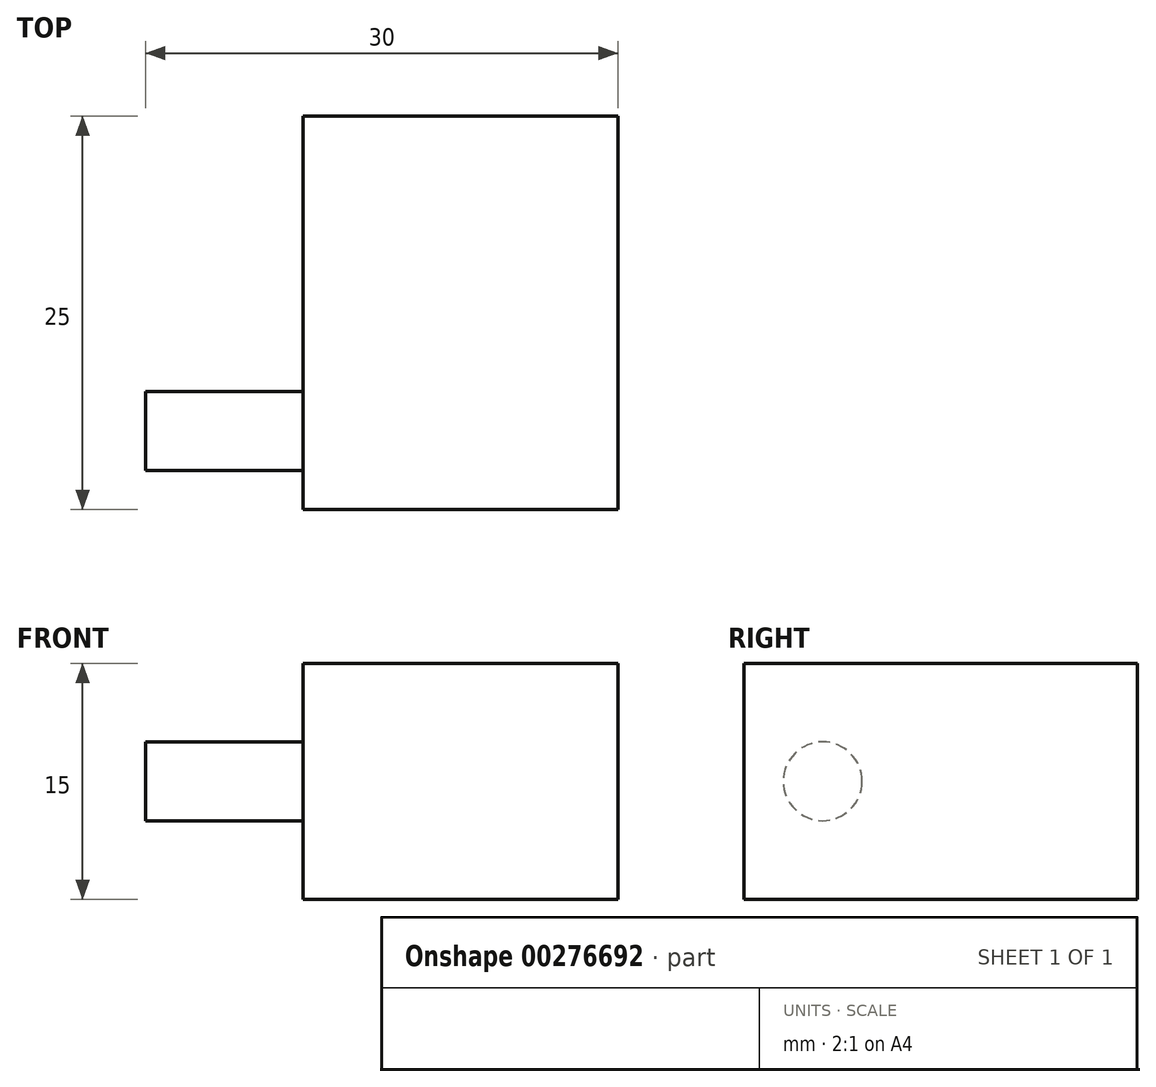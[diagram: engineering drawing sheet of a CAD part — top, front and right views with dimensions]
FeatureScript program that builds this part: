
annotation { "Feature Type Name" : "Feature", "Feature Type Description" : "" }
export const myFeature = defineFeature(function(context is Context, id is Id, definition is map)
    precondition{}
    {
        {
            var Q0;
            Q0=qCreatedBy(makeId("Right.planeOp"),FACE);
            var sketch = newSketch(context, id + "F0", { "sketchPlane" : qUnion([Q0])});
            skLineSegment(sketch, "E0.bottom", {"start": v(-12.5, 7.5) * mm, "end": v(12.5, 7.5) * mm});
            skLineSegment(sketch, "E0.top", {"start": v(-12.5, -7.5) * mm, "end": v(12.5, -7.5) * mm});
            skLineSegment(sketch, "E0.left", {"start": v(-12.5, 7.5) * mm, "end": v(-12.5, -7.5) * mm});
            skLineSegment(sketch, "E0.right", {"start": v(12.5, 7.5) * mm, "end": v(12.5, -7.5) * mm});
            skSolve(sketch);
        }
        {
            var Q0;
            Q0 = qSketchRegion(id + "F0", true);
            extrude(context, id + "F1", {"entities" : qUnion([Q0]), "depth" : 20 * mm});
        }
        {
            var Q0;
            Q0=makeQuery(id+"F1.opExtrude","CAP_FACE",FACE,{"disambiguationData":[OSD([sQuery(id+"F0.wireOp",EDGE,"E0.bottom"),sQuery(id+"F0.wireOp",EDGE,"E0.top"),sQuery(id+"F0.wireOp",EDGE,"E0.left"),sQuery(id+"F0.wireOp",EDGE,"E0.right")])],"isStart":true});
            var sketch = newSketch(context, id + "F2", { "sketchPlane" : qUnion([Q0])});
            skCircle(sketch, "E1", {"center": v(7.5, 0) * mm, "radius": 2.5 * mm});
            skSolve(sketch);
        }
        {
            var Q0;
            Q0 = qSketchRegion(id + "F2", true);
            extrude(context, id + "F3", {"entities" : qUnion([Q0]), "operationType" : NewBodyOperationType.ADD, "depth" : 10 * mm});
        }
    });
